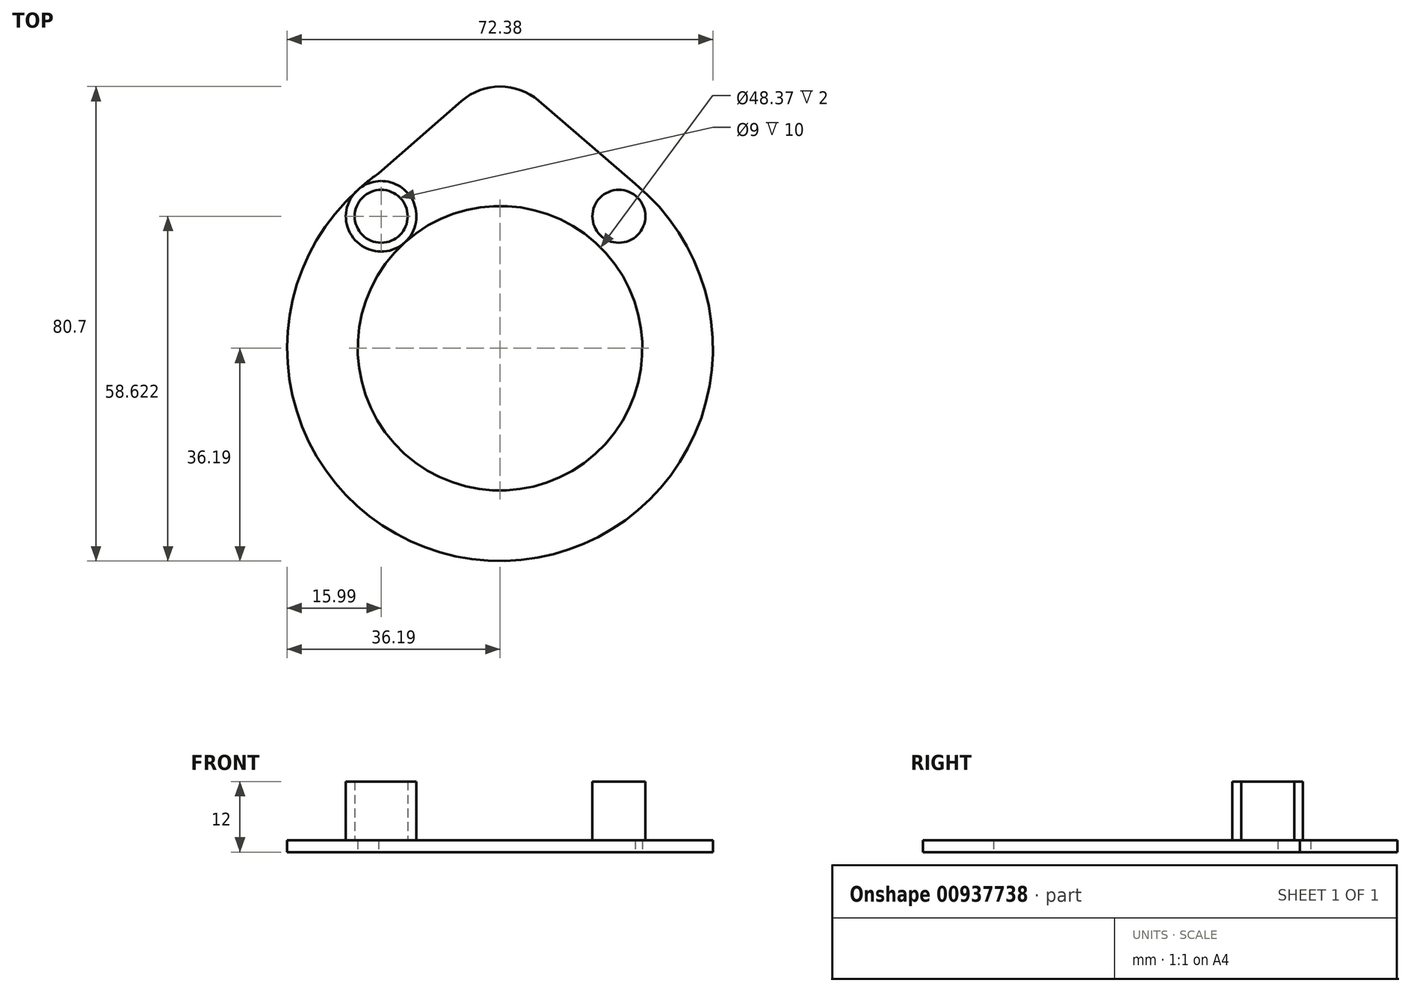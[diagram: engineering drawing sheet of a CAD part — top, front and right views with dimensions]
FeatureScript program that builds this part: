
annotation { "Feature Type Name" : "Feature", "Feature Type Description" : "" }
export const myFeature = defineFeature(function(context is Context, id is Id, definition is map)
    precondition{}
    {
        {
            var Q0;
            Q0=qCreatedBy(makeId("Top.planeOp"),FACE);
            var sketch = newSketch(context, id + "F0", { "sketchPlane" : qUnion([Q0])});
            skCircle(sketch, "E0", {"center": v(0, 0) * mm, "radius": 24.19 * mm});
            skCircle(sketch, "E1.0", {"center": v(0, 0) * mm, "radius": 36.19 * mm});
            skCircle(sketch, "E2.0", {"center": v(0, 0) * mm, "radius": 30.19 * mm, "construction": true});
            skCircle(sketch, "E3", {"center": v(-20.2, 22.43) * mm, "radius": 4.5 * mm});
            skCircle(sketch, "E4", {"center": v(20.2, 22.43) * mm, "radius": 4.5 * mm});
            skCircle(sketch, "E5.0", {"center": v(-20.2, 22.43) * mm, "radius": 6 * mm});
            skCircle(sketch, "E6.0", {"center": v(20.2, 22.43) * mm, "radius": 6 * mm});
            skLineSegment(sketch, "E7", {"start": v(-6.53, 42.04) * mm, "end": v(-26.67, 24.46) * mm});
            skLineSegment(sketch, "E8", {"start": v(6.57, 42.08) * mm, "end": v(24.22, 26.9) * mm});
            skPoint(sketch, "E9.visualSharp", {"position": v(0, 47.74) * mm});
            skArc(sketch, "E9.filletArc", {"start": v(6.57, 42.08) * mm, "mid": v(0.01, 44.5) * mm, "end": v(-6.53, 42.04) * mm});
            skSolve(sketch);
        }
        {
            var Q0;
            Q0 = qSketchRegion(id + "F0", true);
            var Q1;
            Q1=makeQuery(id+"F0.imprint","IMPRINT",FACE,{"disambiguationData":[TD([[makeQuery(id+"F0.imprint","IMPRINT",EDGE,{"derivedFrom":sQuery(id+"F0.wireOp",EDGE,"E3")}),1.0]])]});
            var Q2;
            Q2=makeQuery(id+"F0.imprint","IMPRINT",FACE,{"disambiguationData":[TD([[makeQuery(id+"F0.imprint","IMPRINT",EDGE,{"derivedFrom":sQuery(id+"F0.wireOp",EDGE,"E4")}),1.0]])]});
            var Q3;
            Q3=makeQuery(id+"F0.imprint","IMPRINT",FACE,{"disambiguationData":[TD([[makeQuery(id+"F0.imprint","IMPRINT",EDGE,{"derivedFrom":sQuery(id+"F0.wireOp",EDGE,"E3")}),-1.0]])]});
            extrude(context, id + "F1", {"entities" : qUnion([Q0, Q1, Q2, Q3]), "depth" : 2 * mm, "offsetDistance" : 25 * mm});
        }
        {
            var Q0;
            Q0=makeQuery(id+"F1.opExtrude","CAP_FACE",FACE,{"disambiguationData":[OSD([sQuery(id+"F0.wireOp",EDGE,"E0"),sQuery(id+"F0.wireOp",EDGE,"E1.0")])],"isStart":false});
            var sketch = newSketch(context, id + "F2", { "sketchPlane" : qUnion([Q0])});
            skCircle(sketch, "E10.0", {"center": v(0, 0) * mm, "radius": 30.19 * mm, "construction": true});
            skCircle(sketch, "E11", {"center": v(-20.2, 22.43) * mm, "radius": 4.5 * mm});
            skCircle(sketch, "E12", {"center": v(-20.2, 22.43) * mm, "radius": 6 * mm});
            skCircle(sketch, "E13.MirrorC", {"center": v(20.2, 22.43) * mm, "radius": 4.5 * mm});
            skCircle(sketch, "E14.MirrorC", {"center": v(20.2, 22.43) * mm, "radius": 6 * mm});
            skSolve(sketch);
        }
        {
            var Q0;
            Q0=makeQuery(id+"F2.imprint","IMPRINT",FACE,{"disambiguationData":[TD([[makeQuery(id+"F2.imprint","IMPRINT",EDGE,{"derivedFrom":sQuery(id+"F2.wireOp",EDGE,"E11")}),-1.0]])]});
            var Q1;
            Q1=makeQuery(id+"F2.imprint","IMPRINT",FACE,{"disambiguationData":[TD([[makeQuery(id+"F2.imprint","IMPRINT",EDGE,{"derivedFrom":sQuery(id+"F2.wireOp",EDGE,"E13.MirrorC")}),1.0]])]});
            extrude(context, id + "F3", {"entities" : qUnion([Q0, Q1]), "operationType" : NewBodyOperationType.ADD, "depth" : 10 * mm, "offsetDistance" : 25 * mm});
        }
    });
